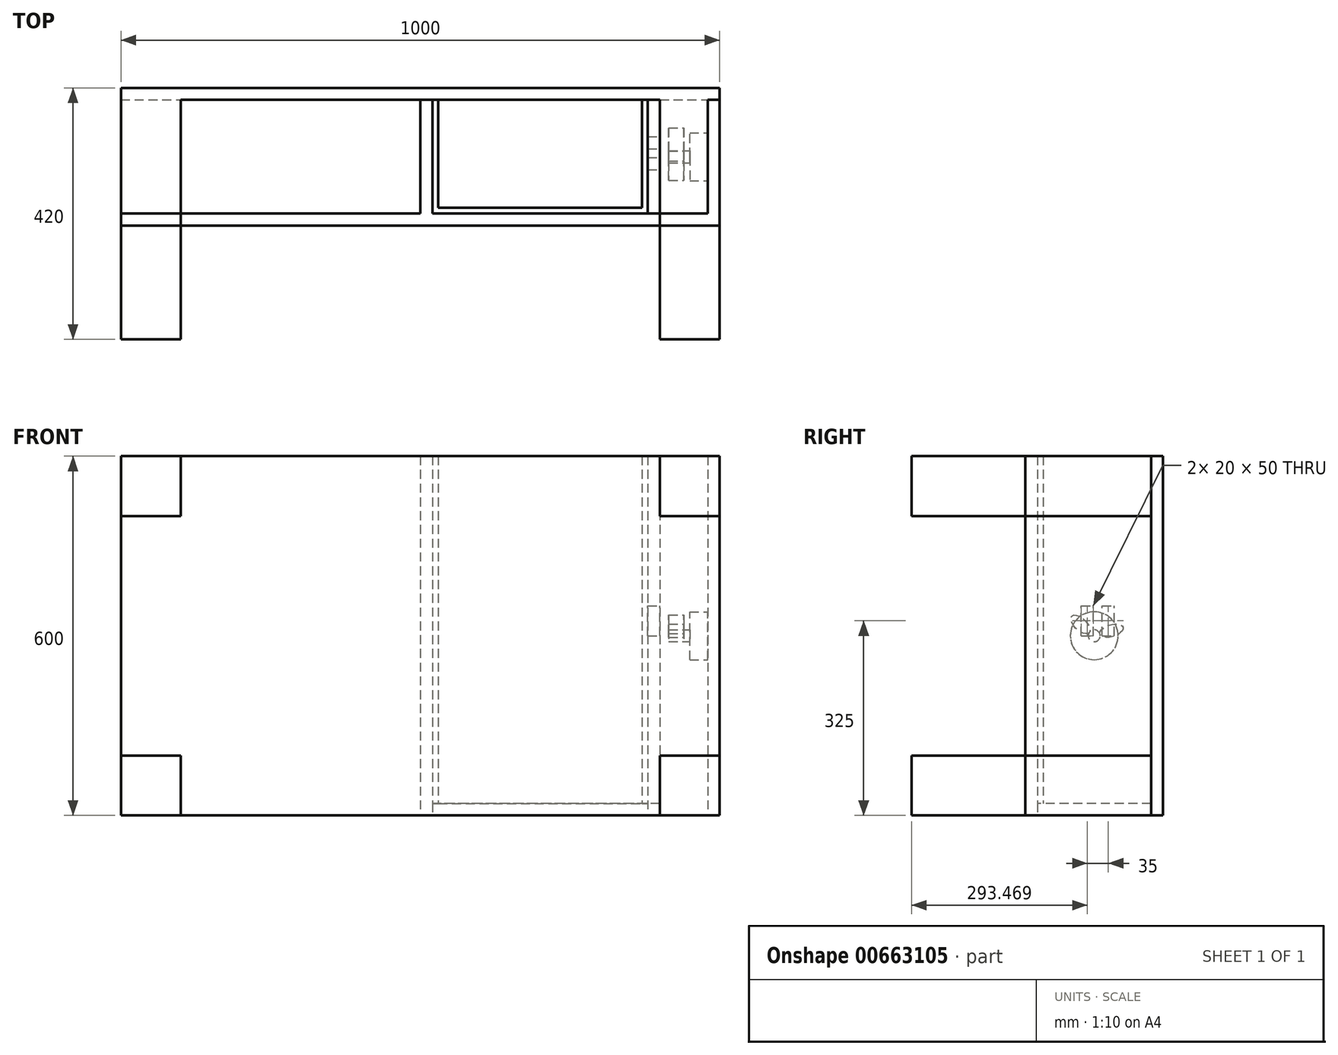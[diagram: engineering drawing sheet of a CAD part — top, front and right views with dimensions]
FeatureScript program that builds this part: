
annotation { "Feature Type Name" : "Feature", "Feature Type Description" : "" }
export const myFeature = defineFeature(function(context is Context, id is Id, definition is map)
    precondition{}
    {
        {
            var Q0;
            Q0=qCreatedBy(makeId("Front.planeOp"),FACE);
            var sketch = newSketch(context, id + "F0", { "sketchPlane" : qUnion([Q0])});
            skLineSegment(sketch, "E0.bottom", {"start": v(-500, 300) * mm, "end": v(500, 300) * mm});
            skLineSegment(sketch, "E0.top", {"start": v(-500, -300) * mm, "end": v(500, -300) * mm});
            skLineSegment(sketch, "E0.left", {"start": v(-500, 300) * mm, "end": v(-500, -300) * mm});
            skLineSegment(sketch, "E0.right", {"start": v(500, 300) * mm, "end": v(500, -300) * mm});
            skSolve(sketch);
        }
        {
            var Q0;
            Q0=makeQuery(id+"F0.imprint","IMPRINT",FACE,{"disambiguationData":[TD([[makeQuery(id+"F0.imprint","IMPRINT",EDGE,{"derivedFrom":sQuery(id+"F0.wireOp",EDGE,"E0.bottom")}),-1.0]])]});
            extrude(context, id + "F1", {"entities" : qUnion([Q0]), "depth" : 20 * mm, "offsetDistance" : 25.4 * mm});
        }
        {
            var Q0;
            Q0=makeQuery(id+"F1.opExtrude","CAP_FACE",FACE,{"disambiguationData":[OSD([sQuery(id+"F0.wireOp",EDGE,"E0.bottom"),sQuery(id+"F0.wireOp",EDGE,"E0.top"),sQuery(id+"F0.wireOp",EDGE,"E0.left"),sQuery(id+"F0.wireOp",EDGE,"E0.right")])],"isStart":false});
            var sketch = newSketch(context, id + "F2", { "sketchPlane" : qUnion([Q0])});
            skLineSegment(sketch, "E1.bottom", {"start": v(400, 300) * mm, "end": v(500, 300) * mm});
            skLineSegment(sketch, "E1.top", {"start": v(400, 200) * mm, "end": v(500, 200) * mm});
            skLineSegment(sketch, "E1.left", {"start": v(400, 300) * mm, "end": v(400, 200) * mm});
            skLineSegment(sketch, "E1.right", {"start": v(500, 300) * mm, "end": v(500, 200) * mm});
            skLineSegment(sketch, "E2.bottom", {"start": v(-500, 200) * mm, "end": v(-400, 200) * mm});
            skLineSegment(sketch, "E2.top", {"start": v(-500, 300) * mm, "end": v(-400, 300) * mm});
            skLineSegment(sketch, "E2.left", {"start": v(-500, 200) * mm, "end": v(-500, 300) * mm});
            skLineSegment(sketch, "E2.right", {"start": v(-400, 200) * mm, "end": v(-400, 300) * mm});
            skLineSegment(sketch, "E3.bottom", {"start": v(400, -300) * mm, "end": v(500, -300) * mm});
            skLineSegment(sketch, "E3.top", {"start": v(400, -200) * mm, "end": v(500, -200) * mm});
            skLineSegment(sketch, "E3.left", {"start": v(400, -300) * mm, "end": v(400, -200) * mm});
            skLineSegment(sketch, "E3.right", {"start": v(500, -300) * mm, "end": v(500, -200) * mm});
            skLineSegment(sketch, "E4.bottom", {"start": v(-500, -300) * mm, "end": v(-400, -300) * mm});
            skLineSegment(sketch, "E4.top", {"start": v(-500, -200) * mm, "end": v(-400, -200) * mm});
            skLineSegment(sketch, "E4.left", {"start": v(-500, -300) * mm, "end": v(-500, -200) * mm});
            skLineSegment(sketch, "E4.right", {"start": v(-400, -300) * mm, "end": v(-400, -200) * mm});
            skSolve(sketch);
        }
        {
            var Q0;
            Q0 = qSketchRegion(id + "F2", true);
            extrude(context, id + "F3", {"entities" : qUnion([Q0]), "operationType" : NewBodyOperationType.ADD, "depth" : 400 * mm, "offsetDistance" : 25.4 * mm});
        }
        {
            var Q0;
            Q0=qCreatedBy(makeId("Top.planeOp"),FACE);
            var sketch = newSketch(context, id + "F4", { "sketchPlane" : qUnion([Q0])});
            skLineSegment(sketch, "E5.bottom", {"start": v(-500, -210) * mm, "end": v(500, -210) * mm});
            skLineSegment(sketch, "E5.top", {"start": v(-500, -230) * mm, "end": v(500, -230) * mm});
            skLineSegment(sketch, "E5.left", {"start": v(-500, -210) * mm, "end": v(-500, -230) * mm});
            skLineSegment(sketch, "E5.right", {"start": v(500, -210) * mm, "end": v(500, -230) * mm});
            skLineSegment(sketch, "E6.bottom", {"start": v(0, -20) * mm, "end": v(20, -20) * mm});
            skLineSegment(sketch, "E6.top", {"start": v(0, -210) * mm, "end": v(20, -210) * mm});
            skLineSegment(sketch, "E6.left", {"start": v(0, -20) * mm, "end": v(0, -210) * mm});
            skLineSegment(sketch, "E6.right", {"start": v(20, -20) * mm, "end": v(20, -210) * mm});
            skLineSegment(sketch, "E7.bottom", {"start": v(480, -20) * mm, "end": v(500, -20) * mm});
            skLineSegment(sketch, "E7.top", {"start": v(480, -210) * mm, "end": v(500, -210) * mm});
            skLineSegment(sketch, "E7.left", {"start": v(480, -20) * mm, "end": v(480, -210) * mm});
            skLineSegment(sketch, "E7.right", {"start": v(500, -20) * mm, "end": v(500, -210) * mm});
            skSolve(sketch);
        }
        {
            var Q0;
            Q0 = qSketchRegion(id + "F4", true);
            extrude(context, id + "F5", {"entities" : qUnion([Q0]), "endBound" : BoundingType.SYMMETRIC, "depth" : 600 * mm, "offsetDistance" : 25.4 * mm, "hasSecondDirection" : true, "secondDirectionOppositeDirection" : true, "secondDirectionDepth" : 300 * mm});
        }
        {
            var Q0;
            Q0=makeQuery(id+"F5.opExtrude","SWEPT_FACE",FACE,{"disambiguationData":[OSD([sQuery(id+"F4.wireOp",EDGE,"E7.left")])]});
            var sketch = newSketch(context, id + "F6", { "sketchPlane" : qUnion([Q0])});
            skCircle(sketch, "E8", {"center": v(115, 0) * mm, "radius": 40 * mm});
            skSolve(sketch);
        }
        {
            var Q0;
            Q0 = qSketchRegion(id + "F6", true);
            extrude(context, id + "F7", {"entities" : qUnion([Q0]), "operationType" : NewBodyOperationType.ADD, "depth" : 30 * mm, "offsetDistance" : 25.4 * mm});
        }
        {
            var Q0;
            Q0=makeQuery(id+"F7.opExtrude","CAP_FACE",FACE,{"disambiguationData":[OSD([sQuery(id+"F6.wireOp",EDGE,"E8")])],"isStart":false});
            var sketch = newSketch(context, id + "F8", { "sketchPlane" : qUnion([Q0])});
            skCircle(sketch, "E9", {"center": v(115, 0) * mm, "radius": 10 * mm});
            skSolve(sketch);
        }
        {
            var Q0;
            Q0=makeQuery(id+"F8.imprint","IMPRINT",FACE,{"disambiguationData":[TD([[makeQuery(id+"F8.imprint","IMPRINT",EDGE,{"derivedFrom":sQuery(id+"F8.wireOp",EDGE,"E9")}),1.0]])]});
            extrude(context, id + "F9", {"entities" : qUnion([Q0]), "operationType" : NewBodyOperationType.ADD, "depth" : 10 * mm, "offsetDistance" : 25.4 * mm});
        }
        {
            var Q0;
            Q0=makeQuery(id+"F9.opExtrude","CAP_FACE",FACE,{"disambiguationData":[OSD([sQuery(id+"F8.wireOp",EDGE,"E9")])],"isStart":false});
            var sketch = newSketch(context, id + "F10", { "sketchPlane" : qUnion([Q0])});
            skEllipse(sketch, "E10", {"center": v(86.23, 8.5) * mm, "majorRadius": 10 * mm, "minorRadius": 20 * mm, "majorAxis": v(0.28, 0.96)});
            skEllipse(sketch, "E11", {"center": v(138.19, 19.04) * mm, "majorRadius": 20 * mm, "minorRadius": 10 * mm, "majorAxis": v(-0.72, -0.7)});
            skEllipse(sketch, "E12", {"center": v(127.64, -27.2) * mm, "majorRadius": 20 * mm, "minorRadius": 10 * mm, "majorAxis": v(-0.42, 0.9)});
            skPoint(sketch, "E13", {"position": v(115, 0) * mm});
            skSolve(sketch);
        }
        {
            var Q0;
            Q0=makeQuery(id+"F10.imprint","IMPRINT",FACE,{"disambiguationData":[TD([[makeQuery(id+"F10.imprint","IMPRINT",EDGE,{"derivedFrom":sQuery(id+"F10.wireOp",EDGE,"E10")}),1.0]])]});
            var Q1;
            Q1=makeQuery(id+"F10.imprint","IMPRINT",FACE,{"disambiguationData":[TD([[makeQuery(id+"F10.imprint","IMPRINT",EDGE,{"derivedFrom":sQuery(id+"F10.wireOp",EDGE,"E11")}),1.0]])]});
            extrude(context, id + "F11", {"entities" : qUnion([Q0, Q1]), "depth" : 25.4 * mm, "offsetDistance" : 25.4 * mm});
        }
        {
            var Q0;
            Q0=sQuery(id+"F10.wireOp",EDGE,"E12");
            extrude(context, id + "F12", {"bodyType" : ToolBodyType.SURFACE, "surfaceEntities" : qUnion([Q0]), "depth" : 25.4 * mm, "offsetDistance" : 25.4 * mm});
        }
        {
            var Q0;
            Q0=makeQuery(id+"F10.imprint","IMPRINT",FACE,{"disambiguationData":[TD([[makeQuery(id+"F10.imprint","IMPRINT",EDGE,{"derivedFrom":makeQuery(id+"F9.opExtrude","CAP_EDGE",EDGE,{"disambiguationData":[OSD([sQuery(id+"F8.wireOp",EDGE,"E9")])],"isStart":false})}),1.0]])]});
            extrude(context, id + "F13", {"entities" : qUnion([Q0]), "depth" : 25.4 * mm, "offsetDistance" : 25.4 * mm});
        }
        {
            var Q0;
            Q0=makeQuery(id+"F3.opExtrude","SWEPT_FACE",FACE,{"disambiguationData":[OSD([sQuery(id+"F2.wireOp",EDGE,"E1.left")])]});
            var sketch = newSketch(context, id + "F14", { "sketchPlane" : qUnion([Q0])});
            skLineSegment(sketch, "E14.bottom", {"start": v(210, 300) * mm, "end": v(20, 300) * mm});
            skLineSegment(sketch, "E14.top", {"start": v(210, -300) * mm, "end": v(20, -300) * mm});
            skLineSegment(sketch, "E14.left", {"start": v(210, 300) * mm, "end": v(210, -300) * mm});
            skLineSegment(sketch, "E14.right", {"start": v(20, 300) * mm, "end": v(20, -300) * mm});
            skLineSegment(sketch, "E15.bottom", {"start": v(136.53, 0) * mm, "end": v(116.53, 0) * mm});
            skLineSegment(sketch, "E15.top", {"start": v(136.53, 50) * mm, "end": v(116.53, 50) * mm});
            skLineSegment(sketch, "E15.left", {"start": v(136.53, 0) * mm, "end": v(136.53, 50) * mm});
            skLineSegment(sketch, "E15.right", {"start": v(116.53, 0) * mm, "end": v(116.53, 50) * mm});
            skLineSegment(sketch, "E16.bottom", {"start": v(101.53, 0) * mm, "end": v(81.53, 0) * mm});
            skLineSegment(sketch, "E16.top", {"start": v(101.53, 50) * mm, "end": v(81.53, 50) * mm});
            skLineSegment(sketch, "E16.left", {"start": v(101.53, 0) * mm, "end": v(101.53, 50) * mm});
            skLineSegment(sketch, "E16.right", {"start": v(81.53, 0) * mm, "end": v(81.53, 50) * mm});
            skLineSegment(sketch, "E17.bottom", {"start": v(116.53, 50) * mm, "end": v(116.53, 50) * mm});
            skLineSegment(sketch, "E17.top", {"start": v(116.53, 50) * mm, "end": v(116.53, 50) * mm});
            skLineSegment(sketch, "E17.left", {"start": v(116.53, 50) * mm, "end": v(116.53, 50) * mm});
            skLineSegment(sketch, "E17.right", {"start": v(116.53, 50) * mm, "end": v(116.53, 50) * mm});
            skSolve(sketch);
        }
        {
            var Q0;
            Q0 = qSketchRegion(id + "F14", true);
            extrude(context, id + "F15", {"entities" : qUnion([Q0]), "depth" : 20 * mm, "offsetDistance" : 25.4 * mm});
        }
        {
            var Q0;
            Q0=makeQuery(id+"F3.boolean.opBoolean","MERGE",FACE,{"derivedFrom":[makeQuery(id+"F1.opExtrude","SWEPT_FACE",FACE,{"disambiguationData":[OSD([sQuery(id+"F0.wireOp",EDGE,"E0.top")])]}),makeQuery(id+"F3.opExtrude","SWEPT_FACE",FACE,{"disambiguationData":[OSD([sQuery(id+"F2.wireOp",EDGE,"E3.bottom")])]}),makeQuery(id+"F3.opExtrude","SWEPT_FACE",FACE,{"disambiguationData":[OSD([sQuery(id+"F2.wireOp",EDGE,"E4.bottom")])]})]});
            var sketch = newSketch(context, id + "F16", { "sketchPlane" : qUnion([Q0])});
            skLineSegment(sketch, "E18.bottom", {"start": v(400, 20) * mm, "end": v(20, 20) * mm});
            skLineSegment(sketch, "E18.top", {"start": v(400, 210) * mm, "end": v(20, 210) * mm});
            skLineSegment(sketch, "E18.left", {"start": v(400, 20) * mm, "end": v(400, 210) * mm});
            skLineSegment(sketch, "E18.right", {"start": v(20, 20) * mm, "end": v(20, 210) * mm});
            skSolve(sketch);
        }
        {
            var Q0;
            Q0 = qSketchRegion(id + "F16", true);
            extrude(context, id + "F17", {"entities" : qUnion([Q0]), "oppositeDirection" : true, "depth" : 20 * mm, "offsetDistance" : 25.4 * mm});
        }
        {
            var Q0;
            Q0=makeQuery(id+"F17.opExtrude","CAP_FACE",FACE,{"disambiguationData":[OSD([sQuery(id+"F16.wireOp",EDGE,"E18.bottom"),sQuery(id+"F16.wireOp",EDGE,"E18.top"),sQuery(id+"F16.wireOp",EDGE,"E18.left"),sQuery(id+"F16.wireOp",EDGE,"E18.right")])],"isStart":false});
            var sketch = newSketch(context, id + "F18", { "sketchPlane" : qUnion([Q0])});
            skLineSegment(sketch, "E19", {"start": v(20, -20) * mm, "end": v(30, -20) * mm});
            skLineSegment(sketch, "E20", {"start": v(30, -20) * mm, "end": v(30, -200) * mm});
            skLineSegment(sketch, "E21", {"start": v(30, -200) * mm, "end": v(370, -200) * mm});
            skLineSegment(sketch, "E22", {"start": v(370, -200) * mm, "end": v(370, -20) * mm});
            skLineSegment(sketch, "E23", {"start": v(370, -20) * mm, "end": v(380, -20) * mm});
            skLineSegment(sketch, "E24", {"start": v(380, -20) * mm, "end": v(380, -210) * mm});
            skLineSegment(sketch, "E25", {"start": v(380, -210) * mm, "end": v(20, -210) * mm});
            skLineSegment(sketch, "E26", {"start": v(20, -210) * mm, "end": v(20, -20) * mm});
            skSolve(sketch);
        }
        {
            var Q0;
            Q0 = qSketchRegion(id + "F18", true);
            extrude(context, id + "F19", {"entities" : qUnion([Q0]), "depth" : 580 * mm, "offsetDistance" : 25.4 * mm});
        }
    });
